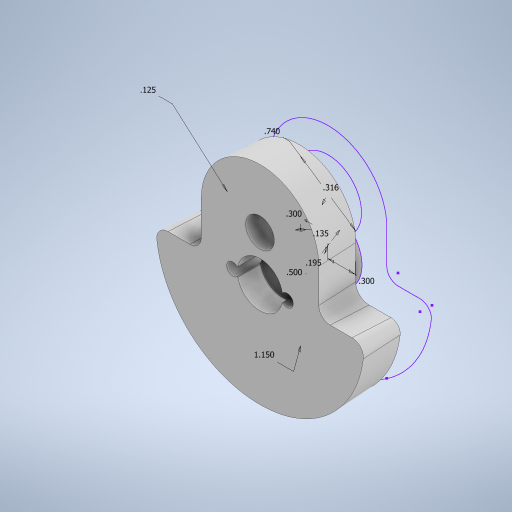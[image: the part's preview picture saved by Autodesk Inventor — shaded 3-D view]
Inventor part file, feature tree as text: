
AUTODESK INVENTOR PART (.ipt)
format: ipt  version: 2023 (Build 270158000, 158)  size: 541,184 bytes
history: native  units: in
note: dims shown in document units (in); Inventor stores cm internally (conversion verified against a paired STEP export)
features: extrude x8, fillet x2, draft x2, sketch x1
ambient origin geometry x8: Origin, YZ Plane, XZ Plane, XY Plane, X Axis, Y Axis, Z Axis, Center Point
bodies: Body1 (feature_tree)
feature tree (13):
  sketch  "Sketch1"  dims[d3=0.866in d15=0.75in d20=0.316in d37=0.75in d44=0.125in d57=0.74in d58=0.75in d59=0.0in d60=0.32in d61=0.0in d62=1.5in d63=0.0in d68=0.125in d70=0.135in d71=0.0206in d72=0.0412in d73=1.15in d76=0.3in d77=0.3in d78=1.0in d79=0.0in d80=1.0in d81=0.0in d84=0.5in d85=0.195in d86=0.5in d87=0.0in d88=0.5in d89=0.0in d90=0.5in d91=0.0in d92=0.005in]
  extrude  "Extrusion9"  Depth=0.005in
  extrude  "Extrusion10"  Depth=0.75in
  extrude  "Extrusion11"  Depth=0.125in
  fillet  "Fillet2"  Radius=0.74in
  draft  "FaceDraft1"
  draft  "FaceDraft2"
  extrude  "Extrusion14"  Depth=0.75in TaperAngle=0.0deg
  extrude  "Extrusion15"  Depth=0.32in TaperAngle=0.0deg
  extrude  "Extrusion17"  Depth=0.005in TaperAngle=0.0deg
  extrude  "Extrusion18"  Depth=0.125in
  extrude  "Extrusion19"  Depth=0.005in
  fillet  "Fillet3"  Radius=0.0206in
